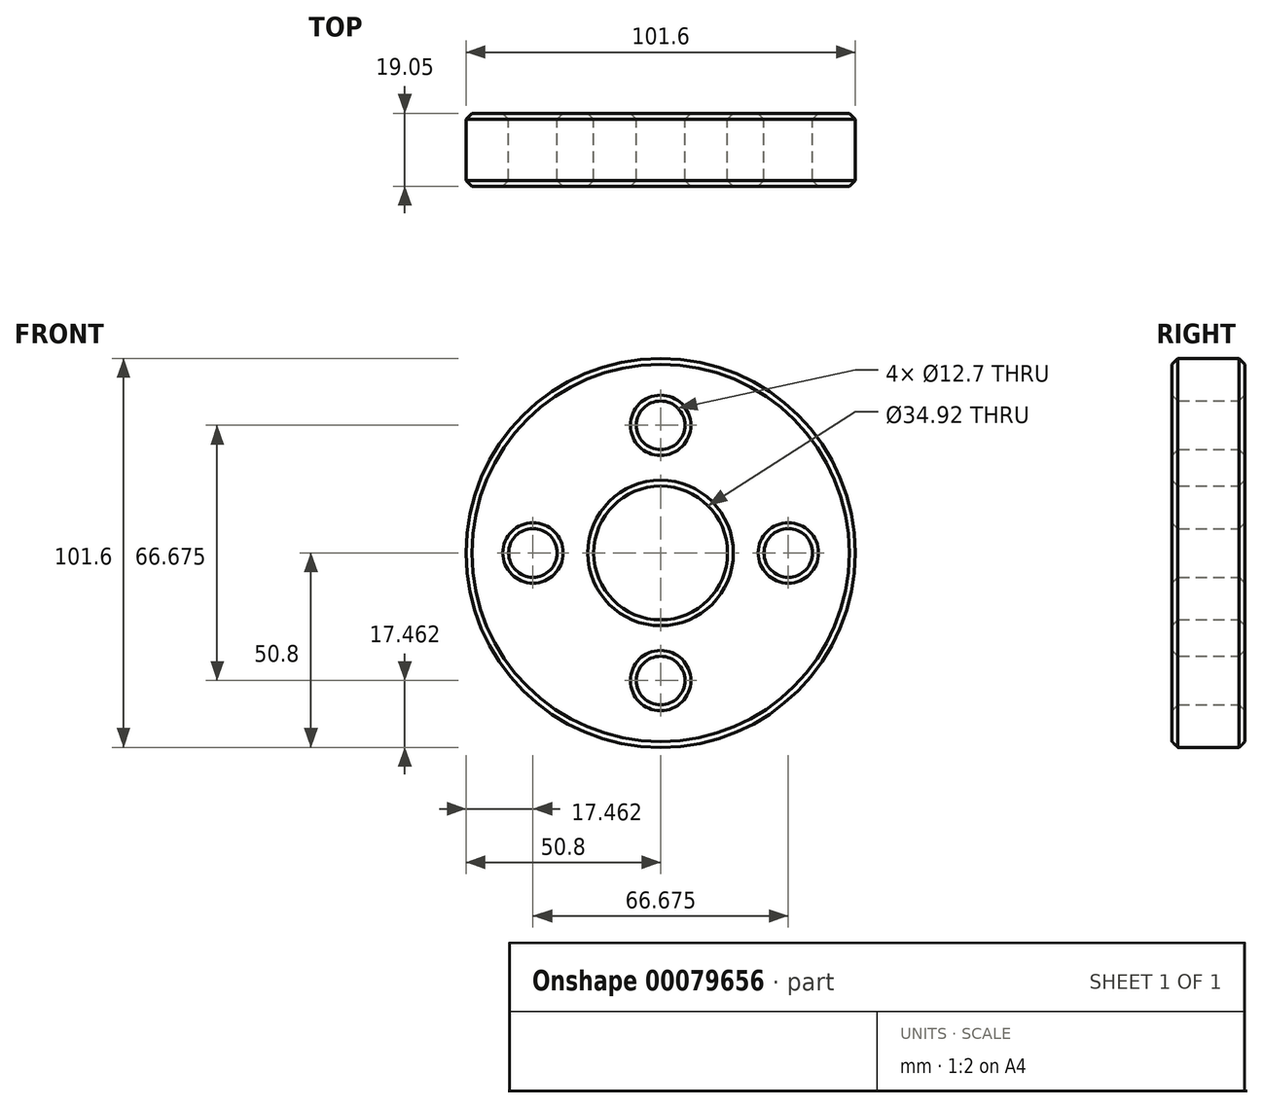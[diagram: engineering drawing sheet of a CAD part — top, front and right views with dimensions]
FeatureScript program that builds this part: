
annotation { "Feature Type Name" : "Feature", "Feature Type Description" : "" }
export const myFeature = defineFeature(function(context is Context, id is Id, definition is map)
    precondition{}
    {
        {
            var Q0;
            Q0=qCreatedBy(makeId("Front.planeOp"),FACE);
            var sketch = newSketch(context, id + "F0", { "sketchPlane" : qUnion([Q0])});
            skCircle(sketch, "E0", {"center": v(0, 0) * mm, "radius": 50.8 * mm});
            skCircle(sketch, "E1", {"center": v(0, 0) * mm, "radius": 17.46 * mm});
            skCircle(sketch, "E2", {"center": v(0, 33.34) * mm, "radius": 6.35 * mm});
            skCircle(sketch, "E3", {"center": v(-33.34, 0) * mm, "radius": 6.35 * mm});
            skCircle(sketch, "E4", {"center": v(0, -33.34) * mm, "radius": 6.35 * mm});
            skCircle(sketch, "E5", {"center": v(33.34, 0) * mm, "radius": 6.35 * mm});
            skSolve(sketch);
        }
        {
            var Q0;
            Q0 = qSketchRegion(id + "F0", true);
            extrude(context, id + "F1", {"entities" : qUnion([Q0]), "depth" : 19.05 * mm});
        }
        {
            var Q0;
            Q0=makeQuery(id+"F1.opExtrude","CAP_EDGE",EDGE,{"disambiguationData":[OSD([sQuery(id+"F0.wireOp",EDGE,"E0")])],"isStart":false});
            chamfer(context, id + "F2", {"entities" : qUnion([Q0]), "width" : 1.52 * mm, "tangentPropagation" : true});
        }
        {
            var Q0;
            Q0=makeQuery(id+"F1.opExtrude","CAP_EDGE",EDGE,{"disambiguationData":[OSD([sQuery(id+"F0.wireOp",EDGE,"E2")])],"isStart":false});
            chamfer(context, id + "F3", {"entities" : qUnion([Q0]), "width" : 1.52 * mm, "tangentPropagation" : true});
        }
        {
            var Q0;
            Q0=makeQuery(id+"F1.opExtrude","CAP_EDGE",EDGE,{"disambiguationData":[OSD([sQuery(id+"F0.wireOp",EDGE,"E3")])],"isStart":false});
            chamfer(context, id + "F4", {"entities" : qUnion([Q0]), "width" : 1.52 * mm, "tangentPropagation" : true});
        }
        {
            var Q0;
            Q0=makeQuery(id+"F1.opExtrude","CAP_EDGE",EDGE,{"disambiguationData":[OSD([sQuery(id+"F0.wireOp",EDGE,"E4")])],"isStart":false});
            chamfer(context, id + "F5", {"entities" : qUnion([Q0]), "width" : 1.52 * mm, "tangentPropagation" : true});
        }
        {
            var Q0;
            Q0=makeQuery(id+"F1.opExtrude","CAP_EDGE",EDGE,{"disambiguationData":[OSD([sQuery(id+"F0.wireOp",EDGE,"E5")])],"isStart":false});
            chamfer(context, id + "F6", {"entities" : qUnion([Q0]), "width" : 1.52 * mm, "tangentPropagation" : true});
        }
        {
            var Q0;
            Q0=makeQuery(id+"F1.opExtrude","CAP_EDGE",EDGE,{"disambiguationData":[OSD([sQuery(id+"F0.wireOp",EDGE,"E1")])],"isStart":false});
            chamfer(context, id + "F7", {"entities" : qUnion([Q0]), "width" : 1.52 * mm, "tangentPropagation" : true});
        }
        {
            var Q0;
            Q0=makeQuery(id+"F1.opExtrude","CAP_EDGE",EDGE,{"disambiguationData":[OSD([sQuery(id+"F0.wireOp",EDGE,"E0")])],"isStart":true});
            chamfer(context, id + "F8", {"entities" : qUnion([Q0]), "width" : 1.52 * mm, "tangentPropagation" : true});
        }
        {
            var Q0;
            Q0=makeQuery(id+"F1.opExtrude","CAP_EDGE",EDGE,{"disambiguationData":[OSD([sQuery(id+"F0.wireOp",EDGE,"E4")])],"isStart":true});
            var Q1;
            Q1=makeQuery(id+"F1.opExtrude","CAP_EDGE",EDGE,{"disambiguationData":[OSD([sQuery(id+"F0.wireOp",EDGE,"E5")])],"isStart":true});
            var Q2;
            Q2=makeQuery(id+"F1.opExtrude","CAP_EDGE",EDGE,{"disambiguationData":[OSD([sQuery(id+"F0.wireOp",EDGE,"E2")])],"isStart":true});
            var Q3;
            Q3=makeQuery(id+"F1.opExtrude","CAP_EDGE",EDGE,{"disambiguationData":[OSD([sQuery(id+"F0.wireOp",EDGE,"E3")])],"isStart":true});
            var Q4;
            Q4=makeQuery(id+"F1.opExtrude","CAP_EDGE",EDGE,{"disambiguationData":[OSD([sQuery(id+"F0.wireOp",EDGE,"E1")])],"isStart":true});
            chamfer(context, id + "F9", {"entities" : qUnion([Q0, Q1, Q2, Q3, Q4]), "width" : 1.52 * mm, "tangentPropagation" : true});
        }
    });
